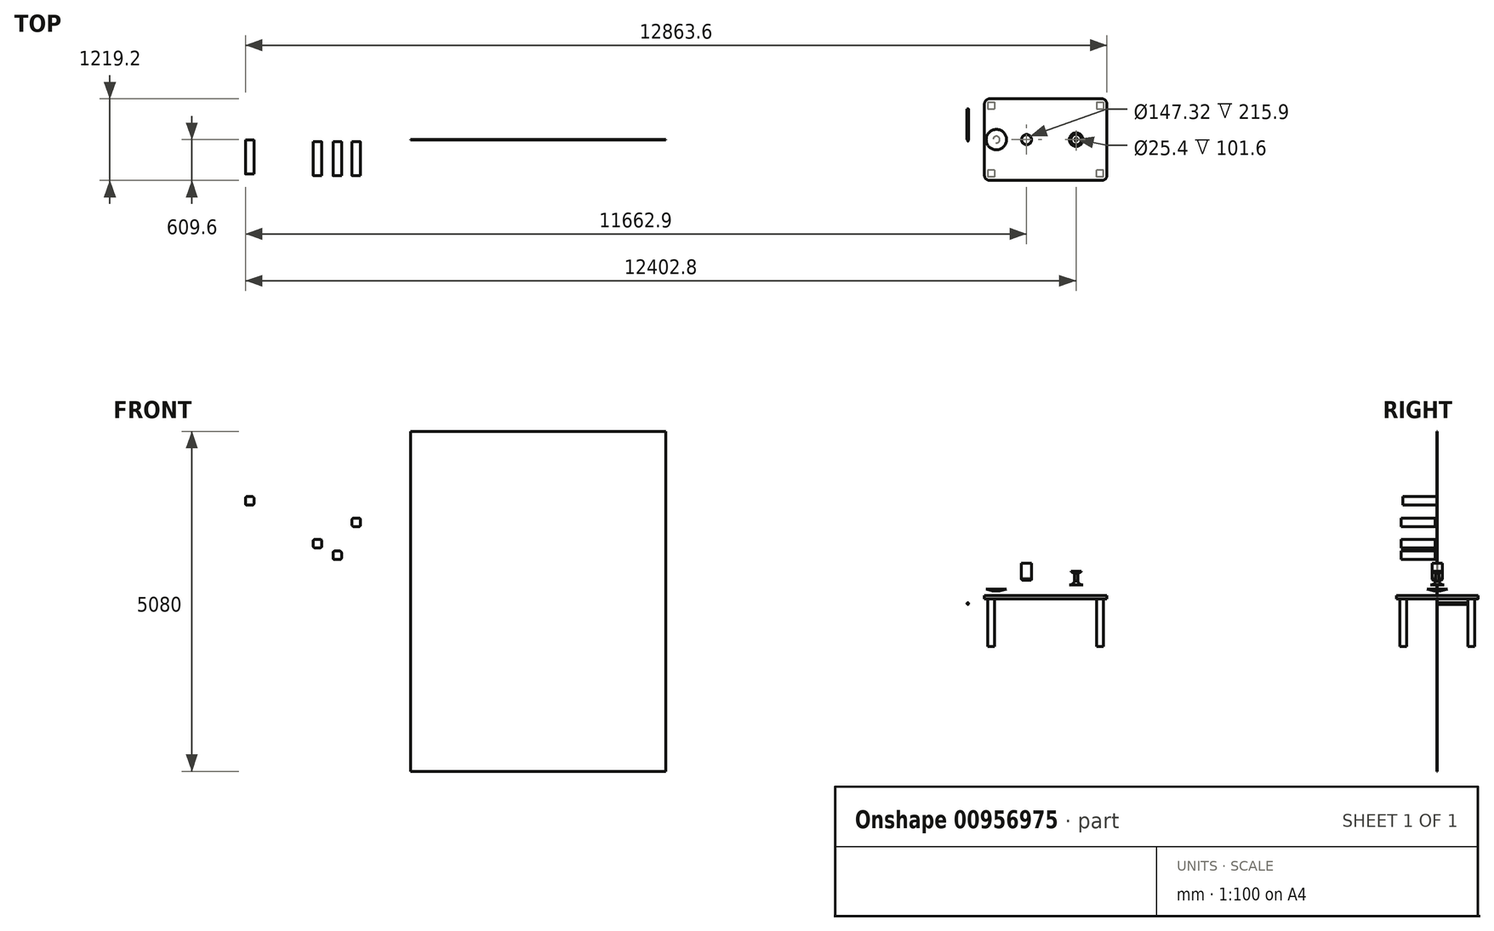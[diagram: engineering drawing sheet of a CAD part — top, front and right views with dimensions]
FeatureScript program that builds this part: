
annotation { "Feature Type Name" : "Feature", "Feature Type Description" : "" }
export const myFeature = defineFeature(function(context is Context, id is Id, definition is map)
    precondition{}
    {
        {
            var Q0;
            Q0=qCreatedBy(makeId("Top.planeOp"),FACE);
            var sketch = newSketch(context, id + "F0", { "sketchPlane" : qUnion([Q0])});
            skLineSegment(sketch, "E0.bottom", {"start": v(-838.2, 609.6) * mm, "end": v(838.2, 609.6) * mm});
            skLineSegment(sketch, "E0.top", {"start": v(-838.2, -609.6) * mm, "end": v(838.2, -609.6) * mm});
            skLineSegment(sketch, "E0.left", {"start": v(-914.4, 533.4) * mm, "end": v(-914.4, -533.4) * mm});
            skLineSegment(sketch, "E0.right", {"start": v(914.4, 533.4) * mm, "end": v(914.4, -533.4) * mm});
            skPoint(sketch, "E0.middle", {"position": v(0, 0) * mm});
            skLineSegment(sketch, "E1.bottom", {"start": v(-863.6, 558.8) * mm, "end": v(-762, 558.8) * mm});
            skLineSegment(sketch, "E1.top", {"start": v(-863.6, 457.2) * mm, "end": v(-762, 457.2) * mm});
            skLineSegment(sketch, "E1.left", {"start": v(-863.6, 558.8) * mm, "end": v(-863.6, 457.2) * mm});
            skLineSegment(sketch, "E1.right", {"start": v(-762, 558.8) * mm, "end": v(-762, 457.2) * mm});
            skLineSegment(sketch, "E2.bottom", {"start": v(762, 558.8) * mm, "end": v(863.6, 558.8) * mm});
            skLineSegment(sketch, "E2.top", {"start": v(762, 457.2) * mm, "end": v(863.6, 457.2) * mm});
            skLineSegment(sketch, "E2.left", {"start": v(762, 558.8) * mm, "end": v(762, 457.2) * mm});
            skLineSegment(sketch, "E2.right", {"start": v(863.6, 558.8) * mm, "end": v(863.6, 457.2) * mm});
            skLineSegment(sketch, "E3.bottom", {"start": v(863.6, -558.8) * mm, "end": v(762, -558.8) * mm});
            skLineSegment(sketch, "E3.top", {"start": v(863.6, -457.2) * mm, "end": v(762, -457.2) * mm});
            skLineSegment(sketch, "E3.left", {"start": v(863.6, -558.8) * mm, "end": v(863.6, -457.2) * mm});
            skLineSegment(sketch, "E3.right", {"start": v(762, -558.8) * mm, "end": v(762, -457.2) * mm});
            skLineSegment(sketch, "E4.bottom", {"start": v(-762, -457.2) * mm, "end": v(-863.6, -457.2) * mm});
            skLineSegment(sketch, "E4.top", {"start": v(-762, -558.8) * mm, "end": v(-863.6, -558.8) * mm});
            skLineSegment(sketch, "E4.left", {"start": v(-762, -457.2) * mm, "end": v(-762, -558.8) * mm});
            skLineSegment(sketch, "E4.right", {"start": v(-863.6, -457.2) * mm, "end": v(-863.6, -558.8) * mm});
            skPoint(sketch, "E5.visualSharp", {"position": v(-914.4, 609.6) * mm});
            skArc(sketch, "E5.filletArc", {"start": v(-838.2, 609.6) * mm, "mid": v(-892.08, 587.28) * mm, "end": v(-914.4, 533.4) * mm});
            skPoint(sketch, "E6.visualSharp", {"position": v(914.4, 609.6) * mm});
            skArc(sketch, "E6.filletArc", {"start": v(914.4, 533.4) * mm, "mid": v(892.08, 587.28) * mm, "end": v(838.2, 609.6) * mm});
            skPoint(sketch, "E7.visualSharp", {"position": v(914.4, -609.6) * mm});
            skArc(sketch, "E7.filletArc", {"start": v(838.2, -609.6) * mm, "mid": v(892.08, -587.28) * mm, "end": v(914.4, -533.4) * mm});
            skPoint(sketch, "E8.visualSharp", {"position": v(-914.4, -609.6) * mm});
            skArc(sketch, "E8.filletArc", {"start": v(-914.4, -533.4) * mm, "mid": v(-892.08, -587.28) * mm, "end": v(-838.2, -609.6) * mm});
            skSolve(sketch);
        }
        {
            var Q0;
            Q0=makeQuery(id+"F0.imprint","IMPRINT",FACE,{"disambiguationData":[TD([[makeQuery(id+"F0.imprint","IMPRINT",EDGE,{"derivedFrom":sQuery(id+"F0.wireOp",EDGE,"E0.bottom")}),-1.0]])]});
            var Q1;
            Q1=makeQuery(id+"F0.imprint","IMPRINT",FACE,{"disambiguationData":[TD([[makeQuery(id+"F0.imprint","IMPRINT",EDGE,{"derivedFrom":sQuery(id+"F0.wireOp",EDGE,"E4.bottom")}),1.0]])]});
            var Q2;
            Q2=makeQuery(id+"F0.imprint","IMPRINT",FACE,{"disambiguationData":[TD([[makeQuery(id+"F0.imprint","IMPRINT",EDGE,{"derivedFrom":sQuery(id+"F0.wireOp",EDGE,"E3.bottom")}),-1.0]])]});
            var Q3;
            Q3=makeQuery(id+"F0.imprint","IMPRINT",FACE,{"disambiguationData":[TD([[makeQuery(id+"F0.imprint","IMPRINT",EDGE,{"derivedFrom":sQuery(id+"F0.wireOp",EDGE,"E2.bottom")}),-1.0]])]});
            var Q4;
            Q4=makeQuery(id+"F0.imprint","IMPRINT",FACE,{"disambiguationData":[TD([[makeQuery(id+"F0.imprint","IMPRINT",EDGE,{"derivedFrom":sQuery(id+"F0.wireOp",EDGE,"E1.bottom")}),-1.0]])]});
            extrude(context, id + "F1", {"entities" : qUnion([Q0, Q1, Q2, Q3, Q4]), "depth" : 50.8 * mm, "offsetDistance" : 25.4 * mm});
        }
        {
            var Q0;
            Q0=makeQuery(id+"F0.imprint","IMPRINT",FACE,{"disambiguationData":[TD([[makeQuery(id+"F0.imprint","IMPRINT",EDGE,{"derivedFrom":sQuery(id+"F0.wireOp",EDGE,"E4.bottom")}),1.0]])]});
            var Q1;
            Q1=makeQuery(id+"F0.imprint","IMPRINT",FACE,{"disambiguationData":[TD([[makeQuery(id+"F0.imprint","IMPRINT",EDGE,{"derivedFrom":sQuery(id+"F0.wireOp",EDGE,"E1.bottom")}),-1.0]])]});
            var Q2;
            Q2=makeQuery(id+"F0.imprint","IMPRINT",FACE,{"disambiguationData":[TD([[makeQuery(id+"F0.imprint","IMPRINT",EDGE,{"derivedFrom":sQuery(id+"F0.wireOp",EDGE,"E2.bottom")}),-1.0]])]});
            var Q3;
            Q3=makeQuery(id+"F0.imprint","IMPRINT",FACE,{"disambiguationData":[TD([[makeQuery(id+"F0.imprint","IMPRINT",EDGE,{"derivedFrom":sQuery(id+"F0.wireOp",EDGE,"E3.bottom")}),-1.0]])]});
            extrude(context, id + "F2", {"entities" : qUnion([Q0, Q1, Q2, Q3]), "operationType" : NewBodyOperationType.ADD, "oppositeDirection" : true, "depth" : 711.2 * mm, "offsetDistance" : 25.4 * mm});
        }
        {
            var Q0;
            Q0=qCreatedBy(makeId("Front.planeOp"),FACE);
            var sketch = newSketch(context, id + "F3", { "sketchPlane" : qUnion([Q0])});
            skLineSegment(sketch, "E9", {"start": v(-286.32, 278.16) * mm, "end": v(-286.32, 532.16) * mm, "construction": true});
            skLineSegment(sketch, "E10.bottom", {"start": v(-286.32, 278.16) * mm, "end": v(-210.12, 278.16) * mm});
            skLineSegment(sketch, "E10.top", {"start": v(-286.32, 316.26) * mm, "end": v(-210.12, 316.26) * mm});
            skLineSegment(sketch, "E10.left", {"start": v(-286.32, 278.16) * mm, "end": v(-286.32, 316.26) * mm});
            skLineSegment(sketch, "E10.right", {"start": v(-210.12, 278.16) * mm, "end": v(-210.12, 316.26) * mm});
            skLineSegment(sketch, "E11.bottom", {"start": v(-210.12, 316.26) * mm, "end": v(-212.66, 316.26) * mm});
            skLineSegment(sketch, "E11.top", {"start": v(-210.12, 532.16) * mm, "end": v(-212.66, 532.16) * mm});
            skLineSegment(sketch, "E11.left", {"start": v(-210.12, 316.26) * mm, "end": v(-210.12, 532.16) * mm});
            skLineSegment(sketch, "E11.right", {"start": v(-212.66, 316.26) * mm, "end": v(-212.66, 532.16) * mm});
            skSolve(sketch);
        }
        {
            var Q0;
            Q0=makeQuery(id+"F3.imprint","IMPRINT",FACE,{"disambiguationData":[TD([[makeQuery(id+"F3.imprint","IMPRINT",EDGE,{"derivedFrom":sQuery(id+"F3.wireOp",EDGE,"E10.bottom")}),1.0]])]});
            var Q1;
            Q1=makeQuery(id+"F3.imprint","IMPRINT",FACE,{"disambiguationData":[TD([[makeQuery(id+"F3.imprint","IMPRINT",EDGE,{"derivedFrom":sQuery(id+"F3.wireOp",EDGE,"E11.top")}),1.0]])]});
            var Q2;
            Q2=sQuery(id+"F3.wireOp",EDGE,"E9");
            revolve(context, id + "F4", {"surfaceOperationType" : NewSurfaceOperationType.NEW, "entities" : qUnion([Q0, Q1]), "axis" : qUnion([Q2]), "revolveType" : RevolveType.FULL});
        }
        {
            var Q0;
            Q0=makeQuery(id+"F4.opRevolve","SWEPT_EDGE",EDGE,{"disambiguationData":[OSD([sQuery(id+"F3.wireOp",EDGE,"E10.bottom"),sQuery(id+"F3.wireOp",EDGE,"E10.right")])]});
            chamfer(context, id + "F5", {"entities" : qUnion([Q0]), "width" : 10.16 * mm, "tangentPropagation" : true});
        }
        {
            var Q0;
            Q0=qCreatedBy(makeId("Front.planeOp"),FACE);
            var sketch = newSketch(context, id + "F6", { "sketchPlane" : qUnion([Q0])});
            skLineSegment(sketch, "E12", {"start": v(-736.83, 117.03) * mm, "end": v(-736.83, 258.84) * mm});
            skLineSegment(sketch, "E13", {"start": v(-736.83, 117.03) * mm, "end": v(-787.63, 117.03) * mm});
            skLineSegment(sketch, "E14", {"start": v(-787.63, 117.03) * mm, "end": v(-889.23, 144.25) * mm});
            skLineSegment(sketch, "E15", {"start": v(-889.23, 144.25) * mm, "end": v(-736.83, 119.57) * mm});
            skSolve(sketch);
        }
        {
            var Q0;
            {var subQ0=sQuery(id+"F6.wireOp",EDGE,"E13");Q0=makeQuery(id+"F6.imprint","IMPRINT",FACE,{"disambiguationData":[TD([[makeQuery(id+"F6.imprint","IMPRINT",EDGE,{"derivedFrom":subQ0}),-1.0]])]});}
            var Q1;
            Q1=sQuery(id+"F6.wireOp",EDGE,"E12");
            revolve(context, id + "F7", {"surfaceOperationType" : NewSurfaceOperationType.NEW, "entities" : qUnion([Q0]), "axis" : qUnion([Q1]), "revolveType" : RevolveType.FULL});
        }
        {
            var Q0;
            Q0=qCreatedBy(makeId("Front.planeOp"),FACE);
            var sketch = newSketch(context, id + "F8", { "sketchPlane" : qUnion([Q0])});
            skCircle(sketch, "E16", {"center": v(-1161.66, -71.9) * mm, "radius": 12.7 * mm});
            skCircle(sketch, "E17", {"center": v(-1161.66, -71.9) * mm, "radius": 1.27 * mm});
            skSolve(sketch);
        }
        {
            var Q0;
            Q0=makeQuery(id+"F8.imprint","IMPRINT",FACE,{"disambiguationData":[TD([[makeQuery(id+"F8.imprint","IMPRINT",EDGE,{"derivedFrom":sQuery(id+"F8.wireOp",EDGE,"E16")}),1.0]])]});
            var Q1;
            Q1=makeQuery(id+"F8.imprint","IMPRINT",FACE,{"disambiguationData":[TD([[makeQuery(id+"F8.imprint","IMPRINT",EDGE,{"derivedFrom":sQuery(id+"F8.wireOp",EDGE,"E17")}),1.0]])]});
            extrude(context, id + "F9", {"entities" : qUnion([Q0, Q1]), "oppositeDirection" : true, "depth" : 457.2 * mm, "offsetDistance" : 25.4 * mm});
        }
        {
            var Q0;
            Q0=makeQuery(id+"F8.imprint","IMPRINT",FACE,{"disambiguationData":[TD([[makeQuery(id+"F8.imprint","IMPRINT",EDGE,{"derivedFrom":sQuery(id+"F8.wireOp",EDGE,"E17")}),1.0]])]});
            extrude(context, id + "F10", {"entities" : qUnion([Q0]), "operationType" : NewBodyOperationType.ADD, "depth" : 25.4 * mm, "offsetDistance" : 25.4 * mm});
        }
        {
            var Q0;
            Q0=makeQuery(id+"F9.opExtrude","CAP_EDGE",EDGE,{"disambiguationData":[OSD([sQuery(id+"F8.wireOp",EDGE,"E16")])],"isStart":true});
            fillet(context, id + "F11", {"entities" : qUnion([Q0]), "radius" : 2.54 * mm, "tangentPropagation" : true, "allowEdgeOverflow" : false});
        }
        {
            var Q0;
            Q0=qCreatedBy(makeId("Front.planeOp"),FACE);
            var sketch = newSketch(context, id + "F12", { "sketchPlane" : qUnion([Q0])});
            skLineSegment(sketch, "E18", {"start": v(453.58, 205.76) * mm, "end": v(453.58, 408.96) * mm});
            skLineSegment(sketch, "E19", {"start": v(453.58, 205.76) * mm, "end": v(351.98, 205.76) * mm});
            skLineSegment(sketch, "E20.bottom", {"start": v(453.58, 260.73) * mm, "end": v(428.18, 260.73) * mm});
            skLineSegment(sketch, "E20.top", {"start": v(453.58, 376.7) * mm, "end": v(428.18, 376.7) * mm});
            skLineSegment(sketch, "E20.left", {"start": v(453.58, 260.73) * mm, "end": v(453.58, 376.7) * mm});
            skLineSegment(sketch, "E20.right", {"start": v(428.18, 260.73) * mm, "end": v(428.18, 376.7) * mm});
            skLineSegment(sketch, "E21.bottom", {"start": v(453.58, 376.7) * mm, "end": v(420.56, 376.7) * mm});
            skLineSegment(sketch, "E21.top", {"start": v(453.58, 389.4) * mm, "end": v(420.56, 389.4) * mm});
            skLineSegment(sketch, "E21.left", {"start": v(453.58, 376.7) * mm, "end": v(453.58, 389.4) * mm});
            skLineSegment(sketch, "E21.right", {"start": v(420.56, 376.7) * mm, "end": v(420.56, 389.4) * mm});
            skLineSegment(sketch, "E22", {"start": v(504.49, 408.96) * mm, "end": v(355.03, 408.96) * mm});
            skArc(sketch, "E23", {"start": v(375.65, 408.96) * mm, "mid": v(396.06, 394.5) * mm, "end": v(420.56, 389.4) * mm});
            skArc(sketch, "E24", {"start": v(351.98, 205.76) * mm, "mid": v(398.96, 220.93) * mm, "end": v(428.18, 260.73) * mm});
            skLineSegment(sketch, "E25", {"start": v(375.65, 408.96) * mm, "end": v(437.07, 389.4) * mm});
            skSolve(sketch);
        }
        {
            var Q0;
            {var subQ3=sQuery(id+"F12.wireOp",EDGE,"E20.top");Q0=makeQuery(id+"F12.imprint","IMPRINT",FACE,{"disambiguationData":[TD([[makeQuery(id+"F12.imprint","IMPRINT",EDGE,{"derivedFrom":subQ3}),-1.0]])]});}
            var Q1;
            {var subQ0=sQuery(id+"F12.wireOp",EDGE,"E20.bottom");Q1=makeQuery(id+"F12.imprint","IMPRINT",FACE,{"disambiguationData":[TD([[makeQuery(id+"F12.imprint","IMPRINT",EDGE,{"derivedFrom":subQ0}),-1.0]])]});}
            var Q2;
            {var subQ2=sQuery(id+"F12.wireOp",EDGE,"E19");Q2=makeQuery(id+"F12.imprint","IMPRINT",FACE,{"disambiguationData":[TD([[makeQuery(id+"F12.imprint","IMPRINT",EDGE,{"derivedFrom":subQ2}),-1.0]])]});}
            var Q3;
            {var subQ2=sQuery(id+"F12.wireOp",EDGE,"E23");Q3=makeQuery(id+"F12.imprint","IMPRINT",FACE,{"disambiguationData":[TD([[makeQuery(id+"F12.imprint","IMPRINT",EDGE,{"derivedFrom":subQ2}),1.0]])]});}
            var Q4;
            Q4=sQuery(id+"F12.wireOp",EDGE,"E18");
            revolve(context, id + "F13", {"surfaceOperationType" : NewSurfaceOperationType.NEW, "entities" : qUnion([Q0, Q1, Q2, Q3]), "axis" : qUnion([Q4]), "revolveType" : RevolveType.FULL});
        }
        {
            var Q0;
            Q0=makeQuery(id+"F13.opRevolve","SWEPT_FACE",FACE,{"disambiguationData":[OSD([sQuery(id+"F12.wireOp",EDGE,"E21.top")])]});
            var sketch = newSketch(context, id + "F14", { "sketchPlane" : qUnion([Q0])});
            skCircle(sketch, "E26", {"center": v(453.58, 0) * mm, "radius": 12.7 * mm});
            skSolve(sketch);
        }
        {
            var Q0;
            Q0=makeQuery(id+"F14.imprint","IMPRINT",FACE,{"disambiguationData":[TD([[makeQuery(id+"F14.imprint","IMPRINT",EDGE,{"derivedFrom":sQuery(id+"F14.wireOp",EDGE,"E26")}),1.0]])]});
            extrude(context, id + "F15", {"entities" : qUnion([Q0]), "operationType" : NewBodyOperationType.REMOVE, "oppositeDirection" : true, "depth" : 101.6 * mm, "offsetDistance" : 25.4 * mm});
        }
        {
            var Q0;
            Q0=qCreatedBy(makeId("Front.planeOp"),FACE);
            var sketch = newSketch(context, id + "F16", { "sketchPlane" : qUnion([Q0])});
            skLineSegment(sketch, "E27.bottom", {"start": v(-5675.56, 2500.27) * mm, "end": v(-9485.56, 2500.27) * mm});
            skLineSegment(sketch, "E27.top", {"start": v(-5675.56, -2579.73) * mm, "end": v(-9485.56, -2579.73) * mm});
            skLineSegment(sketch, "E27.left", {"start": v(-5675.56, 2500.27) * mm, "end": v(-5675.56, -2579.73) * mm});
            skLineSegment(sketch, "E27.right", {"start": v(-9485.56, 2500.27) * mm, "end": v(-9485.56, -2579.73) * mm});
            skSolve(sketch);
        }
        {
            var Q0;
            Q0=qSketchRegion(id+"F16",true);
            extrude(context, id + "F17", {"entities" : qUnion([Q0]), "depth" : 6.35 * mm, "offsetDistance" : 25.4 * mm});
        }
        {
            var Q0;
            Q0=makeQuery(id+"F17.opExtrude","CAP_FACE",FACE,{"disambiguationData":[OSD([sQuery(id+"F16.wireOp",EDGE,"E27.bottom"),sQuery(id+"F16.wireOp",EDGE,"E27.top"),sQuery(id+"F16.wireOp",EDGE,"E27.left"),sQuery(id+"F16.wireOp",EDGE,"E27.right")])],"isStart":false});
            cPlane(context, id + "F18", {"entities" : qUnion([Q0]), "cplaneType" : CPlaneType.OFFSET, "offset" : 25.4 * mm, "width" : 152.4 * mm, "height" : 152.4 * mm});
        }
        {
            var Q0;
            Q0=makeQuery(id+"F17.opExtrude","CAP_FACE",FACE,{"disambiguationData":[OSD([sQuery(id+"F16.wireOp",EDGE,"E27.bottom"),sQuery(id+"F16.wireOp",EDGE,"E27.top"),sQuery(id+"F16.wireOp",EDGE,"E27.left"),sQuery(id+"F16.wireOp",EDGE,"E27.right")])],"isStart":false});
            var sketch = newSketch(context, id + "F19", { "sketchPlane" : qUnion([Q0])});
            skLineSegment(sketch, "E28.bottom", {"start": v(-11949.19, 1525.65) * mm, "end": v(-11822.19, 1525.65) * mm});
            skLineSegment(sketch, "E28.top", {"start": v(-11949.19, 1398.65) * mm, "end": v(-11822.19, 1398.65) * mm});
            skLineSegment(sketch, "E28.left", {"start": v(-11949.19, 1525.65) * mm, "end": v(-11949.19, 1398.65) * mm});
            skLineSegment(sketch, "E28.right", {"start": v(-11822.19, 1525.65) * mm, "end": v(-11822.19, 1398.65) * mm});
            skSolve(sketch);
        }
        {
            var Q0;
            Q0 = qSketchRegion(id + "F19", true);
            extrude(context, id + "F20", {"entities" : qUnion([Q0]), "depth" : 508 * mm, "offsetDistance" : 25.4 * mm});
        }
        {
            var Q0;
            Q0=makeQuery(id+"F20.opExtrude","SWEPT_EDGE",EDGE,{"disambiguationData":[OSD([sQuery(id+"F19.wireOp",EDGE,"E28.bottom"),sQuery(id+"F19.wireOp",EDGE,"E28.right")])]});
            var Q1;
            Q1=makeQuery(id+"F20.opExtrude","SWEPT_EDGE",EDGE,{"disambiguationData":[OSD([sQuery(id+"F19.wireOp",EDGE,"E28.bottom"),sQuery(id+"F19.wireOp",EDGE,"E28.left")])]});
            var Q2;
            Q2=makeQuery(id+"F20.opExtrude","SWEPT_EDGE",EDGE,{"disambiguationData":[OSD([sQuery(id+"F19.wireOp",EDGE,"E28.top"),sQuery(id+"F19.wireOp",EDGE,"E28.left")])]});
            var Q3;
            Q3=makeQuery(id+"F20.opExtrude","SWEPT_EDGE",EDGE,{"disambiguationData":[OSD([sQuery(id+"F19.wireOp",EDGE,"E28.top"),sQuery(id+"F19.wireOp",EDGE,"E28.right")])]});
            fillet(context, id + "F21", {"entities" : qUnion([Q0, Q1, Q2, Q3]), "radius" : 25.4 * mm, "tangentPropagation" : true, "allowEdgeOverflow" : false});
        }
        {
            var Q0;
            Q0=qCreatedBy(id+"F18.planeOp",FACE);
            var sketch = newSketch(context, id + "F22", { "sketchPlane" : qUnion([Q0])});
            skLineSegment(sketch, "E29.bottom", {"start": v(-10356.8, 1204.78) * mm, "end": v(-10229.8, 1204.78) * mm});
            skLineSegment(sketch, "E29.top", {"start": v(-10356.8, 1077.78) * mm, "end": v(-10229.8, 1077.78) * mm});
            skLineSegment(sketch, "E29.left", {"start": v(-10356.8, 1204.78) * mm, "end": v(-10356.8, 1077.78) * mm});
            skLineSegment(sketch, "E29.right", {"start": v(-10229.8, 1204.78) * mm, "end": v(-10229.8, 1077.78) * mm});
            skSolve(sketch);
        }
        {
            var Q0;
            Q0 = qSketchRegion(id + "F22", true);
            extrude(context, id + "F23", {"entities" : qUnion([Q0]), "depth" : 508 * mm, "offsetDistance" : 25.4 * mm});
        }
        {
            var Q0;
            Q0=makeQuery(id+"F23.opExtrude","SWEPT_EDGE",EDGE,{"disambiguationData":[OSD([sQuery(id+"F22.wireOp",EDGE,"E29.bottom"),sQuery(id+"F22.wireOp",EDGE,"E29.right")])]});
            var Q1;
            Q1=makeQuery(id+"F23.opExtrude","SWEPT_EDGE",EDGE,{"disambiguationData":[OSD([sQuery(id+"F22.wireOp",EDGE,"E29.bottom"),sQuery(id+"F22.wireOp",EDGE,"E29.left")])]});
            var Q2;
            Q2=makeQuery(id+"F23.opExtrude","SWEPT_EDGE",EDGE,{"disambiguationData":[OSD([sQuery(id+"F22.wireOp",EDGE,"E29.top"),sQuery(id+"F22.wireOp",EDGE,"E29.right")])]});
            var Q3;
            Q3=makeQuery(id+"F23.opExtrude","SWEPT_EDGE",EDGE,{"disambiguationData":[OSD([sQuery(id+"F22.wireOp",EDGE,"E29.top"),sQuery(id+"F22.wireOp",EDGE,"E29.left")])]});
            var Q4;
            {var subQ0=sQuery(id+"F19.wireOp",EDGE,"E28.top");Q4=makeQuery(id+"F21.opFillet","BLEND_EDGE",EDGE,{"blendedFrom":[makeQuery(id+"F20.opExtrude","SWEPT_EDGE",EDGE,{"disambiguationData":[OSD([subQ0,sQuery(id+"F19.wireOp",EDGE,"E28.left")])]}),makeQuery(id+"F20.opExtrude","SWEPT_FACE",FACE,{"disambiguationData":[OSD([subQ0])]})],"blendedInto":[makeQuery(id+"F20.opExtrude","SWEPT_FACE",FACE,{"disambiguationData":[OSD([subQ0])]})]});}
            var Q5;
            {var subQ0=sQuery(id+"F19.wireOp",EDGE,"E28.left");Q5=makeQuery(id+"F21.opFillet","BLEND_EDGE",EDGE,{"blendedFrom":[makeQuery(id+"F20.opExtrude","SWEPT_EDGE",EDGE,{"disambiguationData":[OSD([sQuery(id+"F19.wireOp",EDGE,"E28.top"),subQ0])]}),makeQuery(id+"F20.opExtrude","SWEPT_FACE",FACE,{"disambiguationData":[OSD([subQ0])]})],"blendedInto":[makeQuery(id+"F20.opExtrude","SWEPT_FACE",FACE,{"disambiguationData":[OSD([subQ0])]})]});}
            fillet(context, id + "F24", {"entities" : qUnion([Q0, Q1, Q2, Q3, Q4, Q5]), "radius" : 25.4 * mm, "tangentPropagation" : true, "allowEdgeOverflow" : false});
        }
        {
            var Q0;
            Q0=qCreatedBy(id+"F18.planeOp",FACE);
            var sketch = newSketch(context, id + "F25", { "sketchPlane" : qUnion([Q0])});
            skLineSegment(sketch, "E30.bottom", {"start": v(-10809.18, 888.02) * mm, "end": v(-10936.18, 888.02) * mm});
            skLineSegment(sketch, "E30.top", {"start": v(-10809.18, 761.02) * mm, "end": v(-10936.18, 761.02) * mm});
            skLineSegment(sketch, "E30.left", {"start": v(-10809.18, 888.02) * mm, "end": v(-10809.18, 761.02) * mm});
            skLineSegment(sketch, "E30.right", {"start": v(-10936.18, 888.02) * mm, "end": v(-10936.18, 761.02) * mm});
            skSolve(sketch);
        }
        {
            var Q0;
            Q0=makeQuery(id+"F25.imprint","IMPRINT",FACE,{"disambiguationData":[TD([[makeQuery(id+"F25.imprint","IMPRINT",EDGE,{"derivedFrom":sQuery(id+"F25.wireOp",EDGE,"E30.bottom")}),1.0]])]});
            extrude(context, id + "F26", {"entities" : qUnion([Q0]), "depth" : 508 * mm, "offsetDistance" : 25.4 * mm});
        }
        {
            var Q0;
            Q0=makeQuery(id+"F26.opExtrude","SWEPT_EDGE",EDGE,{"disambiguationData":[OSD([sQuery(id+"F25.wireOp",EDGE,"E30.top"),sQuery(id+"F25.wireOp",EDGE,"E30.left")])]});
            var Q1;
            Q1=makeQuery(id+"F26.opExtrude","SWEPT_EDGE",EDGE,{"disambiguationData":[OSD([sQuery(id+"F25.wireOp",EDGE,"E30.bottom"),sQuery(id+"F25.wireOp",EDGE,"E30.left")])]});
            var Q2;
            Q2=makeQuery(id+"F26.opExtrude","SWEPT_EDGE",EDGE,{"disambiguationData":[OSD([sQuery(id+"F25.wireOp",EDGE,"E30.bottom"),sQuery(id+"F25.wireOp",EDGE,"E30.right")])]});
            var Q3;
            Q3=makeQuery(id+"F26.opExtrude","SWEPT_EDGE",EDGE,{"disambiguationData":[OSD([sQuery(id+"F25.wireOp",EDGE,"E30.top"),sQuery(id+"F25.wireOp",EDGE,"E30.right")])]});
            fillet(context, id + "F27", {"entities" : qUnion([Q0, Q1, Q2, Q3]), "radius" : 25.4 * mm, "tangentPropagation" : true, "allowEdgeOverflow" : false});
        }
        {
            var Q0;
            Q0=qCreatedBy(id+"F18.planeOp",FACE);
            var sketch = newSketch(context, id + "F28", { "sketchPlane" : qUnion([Q0])});
            skLineSegment(sketch, "E31.bottom", {"start": v(-10514.53, 711.95) * mm, "end": v(-10641.53, 711.95) * mm});
            skLineSegment(sketch, "E31.top", {"start": v(-10514.53, 584.95) * mm, "end": v(-10641.53, 584.95) * mm});
            skLineSegment(sketch, "E31.left", {"start": v(-10514.53, 711.95) * mm, "end": v(-10514.53, 584.95) * mm});
            skLineSegment(sketch, "E31.right", {"start": v(-10641.53, 711.95) * mm, "end": v(-10641.53, 584.95) * mm});
            skSolve(sketch);
        }
        {
            var Q0;
            Q0=makeQuery(id+"F28.imprint","IMPRINT",FACE,{"disambiguationData":[TD([[makeQuery(id+"F28.imprint","IMPRINT",EDGE,{"derivedFrom":sQuery(id+"F28.wireOp",EDGE,"E31.bottom")}),1.0]])]});
            extrude(context, id + "F29", {"entities" : qUnion([Q0]), "depth" : 508 * mm, "offsetDistance" : 25.4 * mm});
        }
        {
            var Q0;
            Q0=makeQuery(id+"F29.opExtrude","SWEPT_EDGE",EDGE,{"disambiguationData":[OSD([sQuery(id+"F28.wireOp",EDGE,"E31.bottom"),sQuery(id+"F28.wireOp",EDGE,"E31.left")])]});
            var Q1;
            Q1=makeQuery(id+"F29.opExtrude","SWEPT_EDGE",EDGE,{"disambiguationData":[OSD([sQuery(id+"F28.wireOp",EDGE,"E31.bottom"),sQuery(id+"F28.wireOp",EDGE,"E31.right")])]});
            var Q2;
            Q2=makeQuery(id+"F29.opExtrude","SWEPT_EDGE",EDGE,{"disambiguationData":[OSD([sQuery(id+"F28.wireOp",EDGE,"E31.top"),sQuery(id+"F28.wireOp",EDGE,"E31.right")])]});
            var Q3;
            Q3=makeQuery(id+"F29.opExtrude","SWEPT_EDGE",EDGE,{"disambiguationData":[OSD([sQuery(id+"F28.wireOp",EDGE,"E31.top"),sQuery(id+"F28.wireOp",EDGE,"E31.left")])]});
            fillet(context, id + "F30", {"entities" : qUnion([Q0, Q1, Q2, Q3]), "radius" : 25.4 * mm, "tangentPropagation" : true, "allowEdgeOverflow" : false});
        }
    });
